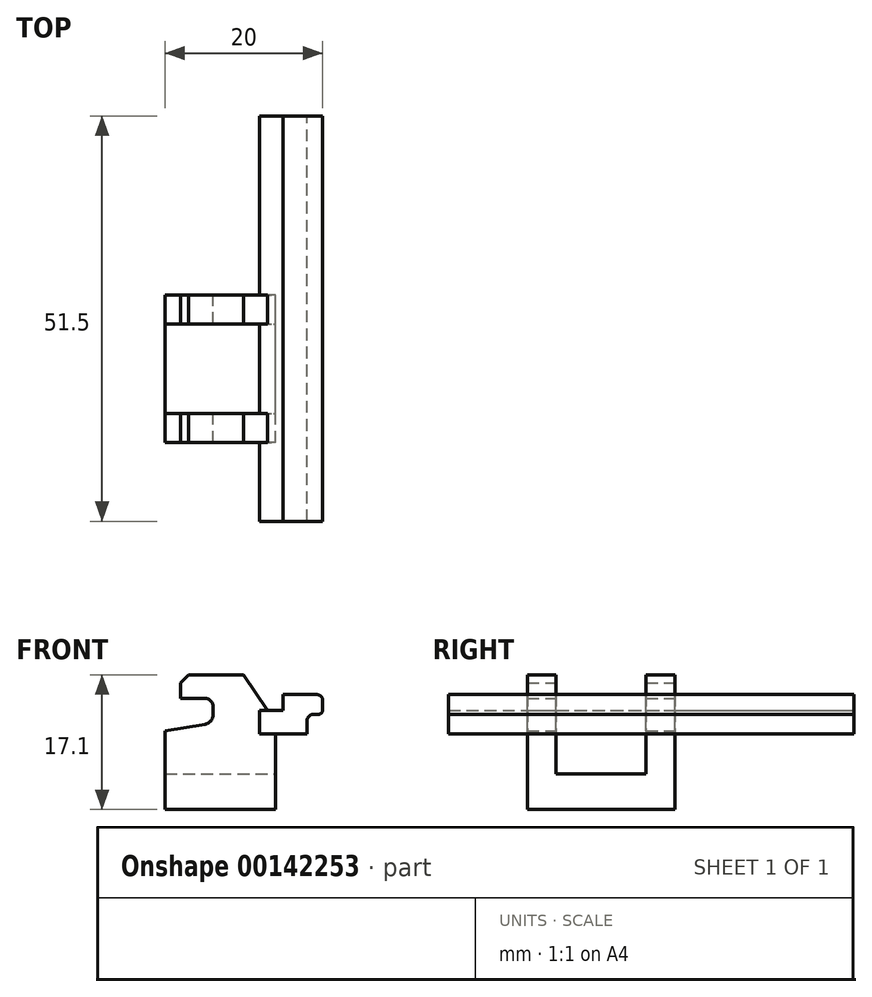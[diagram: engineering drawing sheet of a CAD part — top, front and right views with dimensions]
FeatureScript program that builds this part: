
annotation { "Feature Type Name" : "Feature", "Feature Type Description" : "" }
export const myFeature = defineFeature(function(context is Context, id is Id, definition is map)
    precondition{}
    {
        {
            var Q0;
            Q0=qCreatedBy(makeId("Front.planeOp"),FACE);
            var sketch = newSketch(context, id + "F0", { "sketchPlane" : qUnion([Q0])});
            skLineSegment(sketch, "E0", {"start": v(2, 14.1) * mm, "end": v(2, 17.1) * mm});
            skLineSegment(sketch, "E1", {"start": v(2, 17.1) * mm, "end": v(10, 17.1) * mm});
            skLineSegment(sketch, "E2", {"start": v(10, 17.1) * mm, "end": v(13, 12.6) * mm});
            skLineSegment(sketch, "E3", {"start": v(13, 12.6) * mm, "end": v(14, 12.6) * mm});
            skLineSegment(sketch, "E4", {"start": v(14, 12.6) * mm, "end": v(14, 0) * mm});
            skLineSegment(sketch, "E5", {"start": v(14, 0) * mm, "end": v(0, 0) * mm});
            skLineSegment(sketch, "E6", {"start": v(0, 0) * mm, "end": v(0, 10) * mm});
            skLineSegment(sketch, "E7", {"start": v(0, 10) * mm, "end": v(6.1, 11) * mm});
            skLineSegment(sketch, "E8", {"start": v(6.1, 11) * mm, "end": v(6.1, 13.1) * mm});
            skLineSegment(sketch, "E9", {"start": v(5.1, 14.1) * mm, "end": v(2, 14.1) * mm});
            skPoint(sketch, "E10.visualSharp", {"position": v(6.1, 14.1) * mm});
            skArc(sketch, "E10.filletArc", {"start": v(6.1, 13.1) * mm, "mid": v(5.8, 13.8) * mm, "end": v(5.1, 14.1) * mm});
            skSolve(sketch);
        }
        {
            var Q0;
            Q0 = qSketchRegion(id + "F0", true);
            var Q1;
            Q1=makeQuery(id+"F0.imprint","IMPRINT",FACE,{"disambiguationData":[TD([[makeQuery(id+"F0.imprint","IMPRINT",EDGE,{"derivedFrom":sQuery(id+"F0.wireOp",EDGE,"E0")}),-1.0]])]});
            extrude(context, id + "F1", {"entities" : qUnion([Q0, Q1]), "endBound" : BoundingType.SYMMETRIC, "depth" : 18.75 * mm});
        }
        {
            var Q0;
            {var subQ0=sQuery(id+"F0.wireOp",EDGE,"E8");var subQ1=sQuery(id+"F0.wireOp",EDGE,"E7");Q0=makeQuery(id+"F5.boolean.opBoolean","SPLIT",EDGE,{"disambiguationData":[TD([makeQuery(id+"F5.opExtrude","CAP_FACE",FACE,{"disambiguationData":[OSD([sQuery(id+"F4.wireOp",EDGE,"E11.bottom"),sQuery(id+"F4.wireOp",EDGE,"E11.top"),sQuery(id+"F4.wireOp",EDGE,"E11.left"),sQuery(id+"F4.wireOp",EDGE,"E11.right")])],"isStart":true})])],"derivedFrom":makeQuery(id+"F1.opExtrude","SWEPT_EDGE",EDGE,{"disambiguationData":[OSD([subQ1,subQ0])]})});}
            fillet(context, id + "F2", {"entities" : qUnion([Q0]), "radius" : 1.2 * mm, "tangentPropagation" : true, "allowEdgeOverflow" : false});
        }
        {
            var Q0;
            {var subQ0=sQuery(id+"F0.wireOp",EDGE,"E0");var subQ1=sQuery(id+"F0.wireOp",EDGE,"E1");Q0=makeQuery(id+"F5.boolean.opBoolean","SPLIT",EDGE,{"disambiguationData":[TD([makeQuery(id+"F5.opExtrude","CAP_FACE",FACE,{"disambiguationData":[OSD([sQuery(id+"F4.wireOp",EDGE,"E11.bottom"),sQuery(id+"F4.wireOp",EDGE,"E11.top"),sQuery(id+"F4.wireOp",EDGE,"E11.left"),sQuery(id+"F4.wireOp",EDGE,"E11.right")])],"isStart":true})])],"derivedFrom":makeQuery(id+"F1.opExtrude","SWEPT_EDGE",EDGE,{"disambiguationData":[OSD([subQ0,subQ1])]})});}
            chamfer(context, id + "F3", {"entities" : qUnion([Q0]), "width" : 1 * mm, "tangentPropagation" : true});
        }
        {
            var Q0;
            Q0=qCreatedBy(makeId("Front.planeOp"),FACE);
            var sketch = newSketch(context, id + "F4", { "sketchPlane" : qUnion([Q0])});
            skLineSegment(sketch, "E11.bottom", {"start": v(0, 24.98) * mm, "end": v(29.44, 24.98) * mm});
            skLineSegment(sketch, "E11.top", {"start": v(0, 4.5) * mm, "end": v(29.44, 4.5) * mm});
            skLineSegment(sketch, "E11.left", {"start": v(0, 24.98) * mm, "end": v(0, 4.5) * mm});
            skLineSegment(sketch, "E11.right", {"start": v(29.44, 24.98) * mm, "end": v(29.44, 4.5) * mm});
            skSolve(sketch);
        }
        {
            var Q0;
            Q0=makeQuery(id+"F4.imprint","IMPRINT",FACE,{"disambiguationData":[TD([[makeQuery(id+"F4.imprint","IMPRINT",EDGE,{"derivedFrom":sQuery(id+"F4.wireOp",EDGE,"E11.bottom")}),-1.0]])]});
            extrude(context, id + "F5", {"entities" : qUnion([Q0]), "operationType" : NewBodyOperationType.REMOVE, "endBound" : BoundingType.SYMMETRIC, "oppositeDirection" : true, "depth" : 11.4 * mm});
        }
        {
            var Q0;
            Q0=makeQuery(id+"F1.opExtrude","CAP_FACE",FACE,{"disambiguationData":[OSD([sQuery(id+"F0.wireOp",EDGE,"E0"),sQuery(id+"F0.wireOp",EDGE,"E1"),sQuery(id+"F0.wireOp",EDGE,"E2"),sQuery(id+"F0.wireOp",EDGE,"E3"),sQuery(id+"F0.wireOp",EDGE,"E4"),sQuery(id+"F0.wireOp",EDGE,"E5"),sQuery(id+"F0.wireOp",EDGE,"E6"),sQuery(id+"F0.wireOp",EDGE,"E7"),sQuery(id+"F0.wireOp",EDGE,"E8"),sQuery(id+"F0.wireOp",EDGE,"E9"),sQuery(id+"F0.wireOp",EDGE,"E10.filletArc")])],"isStart":false});
            var sketch = newSketch(context, id + "F6", { "sketchPlane" : qUnion([Q0])});
            skLineSegment(sketch, "E12", {"start": v(18, 9.6) * mm, "end": v(18, 12.1) * mm});
            skLineSegment(sketch, "E13", {"start": v(18, 12.1) * mm, "end": v(20, 12.1) * mm});
            skLineSegment(sketch, "E14", {"start": v(20, 12.1) * mm, "end": v(20, 14.6) * mm});
            skLineSegment(sketch, "E15", {"start": v(20, 14.6) * mm, "end": v(15, 14.6) * mm});
            skLineSegment(sketch, "E16", {"start": v(15, 14.6) * mm, "end": v(15, 9.6) * mm, "construction": true});
            skLineSegment(sketch, "E17", {"start": v(15, 9.6) * mm, "end": v(18, 9.6) * mm});
            skLineSegment(sketch, "E18", {"start": v(15, 9.6) * mm, "end": v(12, 9.6) * mm});
            skLineSegment(sketch, "E19", {"start": v(12, 9.6) * mm, "end": v(12, 12.6) * mm});
            skLineSegment(sketch, "E20", {"start": v(12, 12.6) * mm, "end": v(15, 12.6) * mm});
            skLineSegment(sketch, "E21", {"start": v(15, 12.6) * mm, "end": v(15, 14.6) * mm});
            skSolve(sketch);
        }
        {
            var Q0;
            Q0 = qSketchRegion(id + "F6", true);
            extrude(context, id + "F7", {"entities" : qUnion([Q0]), "operationType" : NewBodyOperationType.ADD, "depth" : 10 * mm, "hasSecondDirection" : true, "secondDirectionOppositeDirection" : true, "secondDirectionDepth" : 41.5 * mm});
        }
        {
            var Q0;
            Q0=makeQuery(id+"F7.opExtrude","SWEPT_EDGE",EDGE,{"disambiguationData":[OSD([sQuery(id+"F6.wireOp",EDGE,"E14"),sQuery(id+"F6.wireOp",EDGE,"E15")])]});
            fillet(context, id + "F8", {"entities" : qUnion([Q0]), "radius" : 0.7 * mm, "tangentPropagation" : true, "allowEdgeOverflow" : false});
        }
        {
            var Q0;
            Q0=makeQuery(id+"F7.opExtrude","SWEPT_EDGE",EDGE,{"disambiguationData":[OSD([sQuery(id+"F6.wireOp",EDGE,"E13"),sQuery(id+"F6.wireOp",EDGE,"E14")])]});
            fillet(context, id + "F9", {"entities" : qUnion([Q0]), "radius" : 0.5 * mm, "tangentPropagation" : true, "allowEdgeOverflow" : false});
        }
        {
            var Q0;
            Q0=makeQuery(id+"F7.opExtrude","SWEPT_EDGE",EDGE,{"disambiguationData":[OSD([sQuery(id+"F6.wireOp",EDGE,"E12"),sQuery(id+"F6.wireOp",EDGE,"E13")])]});
            fillet(context, id + "F10", {"entities" : qUnion([Q0]), "radius" : 0.9 * mm, "tangentPropagation" : true, "allowEdgeOverflow" : false});
        }
    });
